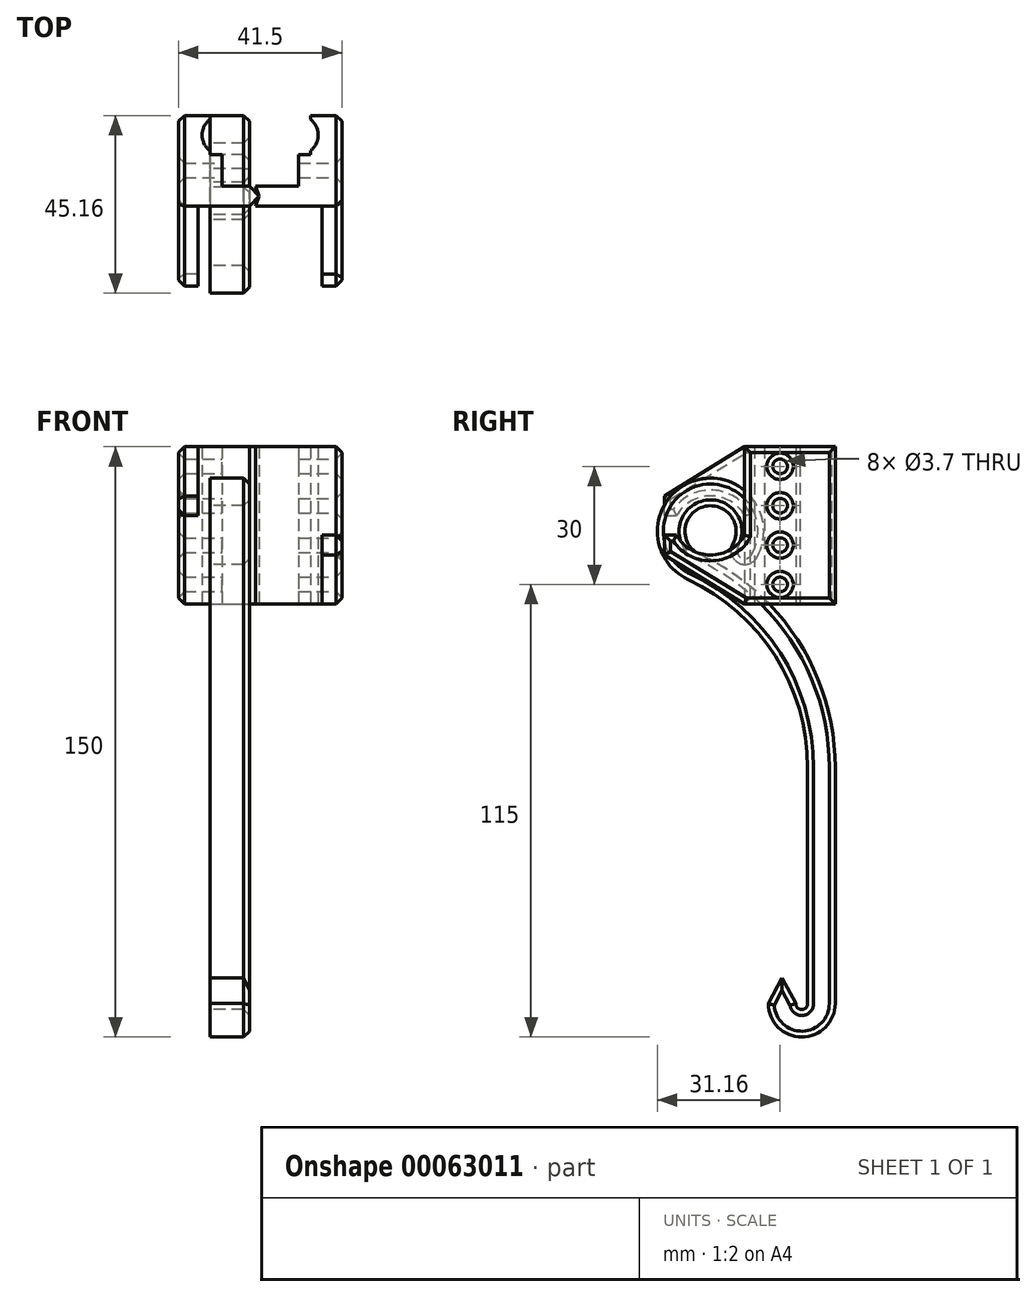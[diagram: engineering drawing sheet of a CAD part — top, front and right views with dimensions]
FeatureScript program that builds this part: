
annotation { "Feature Type Name" : "Feature", "Feature Type Description" : "" }
export const myFeature = defineFeature(function(context is Context, id is Id, definition is map)
    precondition{}
    {
        {
            var Q0;
            Q0=qCreatedBy(makeId("Top.planeOp"),FACE);
            var sketch = newSketch(context, id + "F0", { "sketchPlane" : qUnion([Q0])});
            skLineSegment(sketch, "E0", {"start": v(0, 0) * mm, "end": v(-50, 0) * mm, "construction": true});
            skLineSegment(sketch, "E1", {"start": v(-50, 0) * mm, "end": v(-50, 20) * mm, "construction": true});
            skLineSegment(sketch, "E2", {"start": v(-50, 20) * mm, "end": v(25.5, 20) * mm, "construction": true});
            skLineSegment(sketch, "E3", {"start": v(25.5, 20) * mm, "end": v(25.5, -10) * mm, "construction": true});
            skLineSegment(sketch, "E4", {"start": v(25.5, -10) * mm, "end": v(0, -10) * mm, "construction": true});
            skLineSegment(sketch, "E5", {"start": v(0, -10) * mm, "end": v(0, 0) * mm, "construction": true});
            skLineSegment(sketch, "E6", {"start": v(0, 0) * mm, "end": v(-8, 0) * mm});
            skLineSegment(sketch, "E7", {"start": v(-8, 0) * mm, "end": v(-8, -23) * mm});
            skLineSegment(sketch, "E8", {"start": v(-8, -23) * mm, "end": v(10, -23) * mm});
            skLineSegment(sketch, "E9", {"start": v(10, -23) * mm, "end": v(12.5, -20.5) * mm});
            skLineSegment(sketch, "E10", {"start": v(12.5, -20.5) * mm, "end": v(10, -18) * mm});
            skLineSegment(sketch, "E11", {"start": v(0, -10) * mm, "end": v(3, -10) * mm});
            skLineSegment(sketch, "E12", {"start": v(3, -10) * mm, "end": v(3, -18) * mm});
            skLineSegment(sketch, "E13", {"start": v(3, -18) * mm, "end": v(10, -18) * mm});
            skLineSegment(sketch, "E14", {"start": v(12.5, -20.5) * mm, "end": v(11.6, -18) * mm});
            skLineSegment(sketch, "E15", {"start": v(11.6, -18) * mm, "end": v(22.5, -18) * mm});
            skLineSegment(sketch, "E16", {"start": v(22.5, -18) * mm, "end": v(22.5, -10) * mm});
            skLineSegment(sketch, "E17", {"start": v(22.5, -10) * mm, "end": v(25.5, -10) * mm});
            skLineSegment(sketch, "E18", {"start": v(25.5, 0) * mm, "end": v(33.5, 0) * mm});
            skLineSegment(sketch, "E19", {"start": v(33.5, 0) * mm, "end": v(33.5, -23) * mm});
            skLineSegment(sketch, "E20", {"start": v(33.5, -23) * mm, "end": v(11.6, -23) * mm});
            skLineSegment(sketch, "E21", {"start": v(11.6, -23) * mm, "end": v(12.5, -20.5) * mm});
            skLineSegment(sketch, "E22", {"start": v(25.5, 0) * mm, "end": v(25.5, -1) * mm});
            skLineSegment(sketch, "E23", {"start": v(0, 0) * mm, "end": v(0, -1) * mm});
            skCircle(sketch, "E24", {"center": v(3, -5) * mm, "radius": 5 * mm, "construction": true});
            skCircle(sketch, "E25", {"center": v(22.5, -5) * mm, "radius": 5 * mm, "construction": true});
            skArc(sketch, "E26", {"start": v(0, -1) * mm, "mid": v(-2, -5) * mm, "end": v(0, -9) * mm});
            skArc(sketch, "E27", {"start": v(25.5, -9) * mm, "mid": v(27.5, -5) * mm, "end": v(25.5, -1) * mm});
            skLineSegment(sketch, "E28.trimOffspring", {"start": v(0, -9) * mm, "end": v(0, -10) * mm});
            skLineSegment(sketch, "E29.trimOffspring", {"start": v(25.5, -9) * mm, "end": v(25.5, -10) * mm});
            skSolve(sketch);
        }
        {
            var Q0;
            Q0 = qSketchRegion(id + "F0", true);
            extrude(context, id + "F1", {"entities" : qUnion([Q0]), "depth" : 40 * mm});
        }
        {
            var Q0;
            Q0=makeQuery(id+"F1.opExtrude","SWEPT_FACE",FACE,{"disambiguationData":[OSD([sQuery(id+"F0.wireOp",EDGE,"E19")])]});
            var sketch = newSketch(context, id + "F2", { "sketchPlane" : qUnion([Q0])});
            skArc(sketch, "E30", {"start": v(-40.32, 17.5) * mm, "mid": v(-31.66, 12.5) * mm, "end": v(-23, 17.5) * mm});
            skArc(sketch, "E31", {"start": v(-23, 22.5) * mm, "mid": v(-31.66, 27.5) * mm, "end": v(-40.32, 22.5) * mm});
            skLineSegment(sketch, "E32", {"start": v(-40.32, 17.5) * mm, "end": v(-31.66, 22.5) * mm, "construction": true});
            skLineSegment(sketch, "E33", {"start": v(-23, 17.5) * mm, "end": v(-31.66, 22.5) * mm, "construction": true});
            skLineSegment(sketch, "E34", {"start": v(-40.32, 17.5) * mm, "end": v(-43.32, 17.5) * mm});
            skLineSegment(sketch, "E35", {"start": v(-43.32, 17.5) * mm, "end": v(-43.32, 12.5) * mm});
            skLineSegment(sketch, "E36", {"start": v(-43.32, 12.5) * mm, "end": v(-23, 0) * mm});
            skLineSegment(sketch, "E37", {"start": v(-23, 0) * mm, "end": v(-23, 17.5) * mm});
            skLineSegment(sketch, "E38", {"start": v(-40.32, 22.5) * mm, "end": v(-43.32, 22.5) * mm});
            skLineSegment(sketch, "E39", {"start": v(-43.32, 22.5) * mm, "end": v(-43.32, 27.5) * mm});
            skLineSegment(sketch, "E40", {"start": v(-43.32, 27.5) * mm, "end": v(-23, 40) * mm});
            skPoint(sketch, "E41", {"position": v(-31.66, 27.5) * mm});
            skPoint(sketch, "E42", {"position": v(-31.66, 12.5) * mm});
            skLineSegment(sketch, "E43", {"start": v(-23, 22.5) * mm, "end": v(-23, 40) * mm});
            skSolve(sketch);
        }
        {
            var Q0;
            Q0=makeQuery(id+"F1.opExtrude","SWEPT_FACE",FACE,{"disambiguationData":[OSD([sQuery(id+"F0.wireOp",EDGE,"E7")])]});
            var sketch = newSketch(context, id + "F3", { "sketchPlane" : qUnion([Q0])});
            skLineSegment(sketch, "E44.0", {"start": v(23, 22.5) * mm, "end": v(23, 40) * mm});
            skLineSegment(sketch, "E44.1", {"start": v(43.32, 27.5) * mm, "end": v(23, 40) * mm});
            skArc(sketch, "E44.2", {"start": v(23, 22.5) * mm, "mid": v(31.66, 27.5) * mm, "end": v(40.32, 22.5) * mm});
            skLineSegment(sketch, "E44.3", {"start": v(40.32, 22.5) * mm, "end": v(43.32, 22.5) * mm});
            skLineSegment(sketch, "E44.4", {"start": v(43.32, 22.5) * mm, "end": v(43.32, 27.5) * mm});
            skSolve(sketch);
        }
        {
            var Q0;
            Q0 = qSketchRegion(id + "F3", true);
            extrude(context, id + "F4", {"entities" : qUnion([Q0]), "operationType" : NewBodyOperationType.ADD, "oppositeDirection" : true, "depth" : 5 * mm});
        }
        {
            var Q0;
            Q0=makeQuery(id+"F2.imprint","IMPRINT",FACE,{"disambiguationData":[TD([[makeQuery(id+"F2.imprint","IMPRINT",EDGE,{"derivedFrom":sQuery(id+"F2.wireOp",EDGE,"E30")}),-1.0]])]});
            var Q1;
            Q1=sQuery(id+"F2.wireOp",EDGE,"E30");
            var Q2;
            Q2=sQuery(id+"F2.wireOp",EDGE,"E34");
            var Q3;
            Q3=sQuery(id+"F2.wireOp",EDGE,"E35");
            var Q4;
            Q4=sQuery(id+"F2.wireOp",EDGE,"E36");
            var Q5;
            Q5=sQuery(id+"F2.wireOp",EDGE,"E37");
            extrude(context, id + "F5", {"entities" : qUnion([Q0]), "operationType" : NewBodyOperationType.ADD, "surfaceEntities" : qUnion([Q1, Q2, Q3, Q4, Q5]), "oppositeDirection" : true, "depth" : 5 * mm});
        }
        {
            var Q0;
            Q0=makeQuery(id+"F1.opExtrude","SWEPT_FACE",FACE,{"disambiguationData":[OSD([sQuery(id+"F0.wireOp",EDGE,"E12")])]});
            var sketch = newSketch(context, id + "F6", { "sketchPlane" : qUnion([Q0])});
            skCircle(sketch, "E45", {"center": v(-14, 35) * mm, "radius": 1.85 * mm});
            skCircle(sketch, "E46", {"center": v(-14, 25) * mm, "radius": 1.85 * mm});
            skCircle(sketch, "E47", {"center": v(-14, 15) * mm, "radius": 1.85 * mm});
            skCircle(sketch, "E48", {"center": v(-14, 5) * mm, "radius": 1.85 * mm});
            skLineSegment(sketch, "E49", {"start": v(-14, 0) * mm, "end": v(-14, 5) * mm, "construction": true});
            skLineSegment(sketch, "E50", {"start": v(-14, 15) * mm, "end": v(-14, 5) * mm, "construction": true});
            skLineSegment(sketch, "E51", {"start": v(-14, 15) * mm, "end": v(-14, 25) * mm, "construction": true});
            skLineSegment(sketch, "E52", {"start": v(-14, 35) * mm, "end": v(-14, 25) * mm, "construction": true});
            skLineSegment(sketch, "E53", {"start": v(-14, 35) * mm, "end": v(-14, 40) * mm, "construction": true});
            skSolve(sketch);
        }
        {
            var Q0;
            Q0 = qSketchRegion(id + "F6", true);
            extrude(context, id + "F7", {"entities" : qUnion([Q0]), "operationType" : NewBodyOperationType.REMOVE, "endBound" : BoundingType.THROUGH_ALL, "oppositeDirection" : true, "depth" : 25 * mm, "hasSecondDirection" : true, "secondDirectionBound" : SecondDirectionBoundingType.THROUGH_ALL, "secondDirectionOppositeDirection" : false, "secondDirectionDepth" : 25 * mm});
        }
        {
            var Q0;
            Q0=makeQuery(id+"F5.boolean.opBoolean","MERGE",FACE,{"derivedFrom":[makeQuery(id+"F1.opExtrude","SWEPT_FACE",FACE,{"disambiguationData":[OSD([sQuery(id+"F0.wireOp",EDGE,"E19")])]}),makeQuery(id+"F5.opExtrude","CAP_FACE",FACE,{"disambiguationData":[OSD([sQuery(id+"F2.wireOp",EDGE,"E30"),sQuery(id+"F2.wireOp",EDGE,"E34"),sQuery(id+"F2.wireOp",EDGE,"E35"),sQuery(id+"F2.wireOp",EDGE,"E36"),sQuery(id+"F2.wireOp",EDGE,"E37")])],"isStart":true})]});
            var Q1;
            Q1=makeQuery(id+"F4.boolean.opBoolean","MERGE",FACE,{"derivedFrom":[makeQuery(id+"F1.opExtrude","SWEPT_FACE",FACE,{"disambiguationData":[OSD([sQuery(id+"F0.wireOp",EDGE,"E7")])]}),makeQuery(id+"F4.opExtrude","CAP_FACE",FACE,{"disambiguationData":[OSD([sQuery(id+"F3.wireOp",EDGE,"E44.0"),sQuery(id+"F3.wireOp",EDGE,"E44.1"),sQuery(id+"F3.wireOp",EDGE,"E44.2"),sQuery(id+"F3.wireOp",EDGE,"E44.3"),sQuery(id+"F3.wireOp",EDGE,"E44.4")])],"isStart":true})]});
            chamfer(context, id + "F8", {"entities" : qUnion([Q0, Q1]), "width" : 1.5 * mm, "tangentPropagation" : true});
        }
        {
            var Q0;
            Q0=qCreatedBy(makeId("Right.planeOp"),FACE);
            var sketch = newSketch(context, id + "F9", { "sketchPlane" : qUnion([Q0])});
            skCircle(sketch, "E54", {"center": v(-31.66, 18.5) * mm, "radius": 6 * mm});
            skPoint(sketch, "E55", {"position": v(-31.66, 12.5) * mm});
            skLineSegment(sketch, "E56", {"start": v(-40.32, 17.5) * mm, "end": v(-23, 17.5) * mm, "construction": true});
            skPoint(sketch, "E57", {"position": v(-31.66, 17.5) * mm});
            skArc(sketch, "E58", {"start": v(-19.91, 11.85) * mm, "mid": v(-35.76, 31.36) * mm, "end": v(-37.38, 6.27) * mm});
            skArc(sketch, "E59", {"start": v(-26, 15.3) * mm, "mid": v(-33.64, 24.7) * mm, "end": v(-34.42, 12.61) * mm});
            skArc(sketch, "E60", {"start": v(-37.38, 6.27) * mm, "mid": v(-15.24, -13.2) * mm, "end": v(-7, -41.5) * mm});
            skArc(sketch, "E61", {"start": v(-34.42, 12.61) * mm, "mid": v(-9.33, -9.43) * mm, "end": v(0, -41.5) * mm});
            skArc(sketch, "E62", {"start": v(-19.91, 11.85) * mm, "mid": v(-24.68, 10.53) * mm, "end": v(-26, 15.3) * mm});
            skLineSegment(sketch, "E63", {"start": v(0, -41.5) * mm, "end": v(0, -101.5) * mm});
            skLineSegment(sketch, "E64", {"start": v(-7, -41.5) * mm, "end": v(-7, -101.5) * mm});
            skArc(sketch, "E65", {"start": v(-10, -101.5) * mm, "mid": v(-8.5, -103) * mm, "end": v(-7, -101.5) * mm});
            skArc(sketch, "E66", {"start": v(-17, -101.5) * mm, "mid": v(-8.5, -110) * mm, "end": v(0, -101.5) * mm});
            skPoint(sketch, "E67", {"position": v(-8.5, -110) * mm});
            skPoint(sketch, "E68", {"position": v(-24.68, 10.53) * mm});
            skLineSegment(sketch, "E69", {"start": v(-22.96, 13.57) * mm, "end": v(-24.68, 10.53) * mm, "construction": true});
            skLineSegment(sketch, "E70", {"start": v(-24.68, 10.53) * mm, "end": v(-26.16, 7.92) * mm, "construction": true});
            skPoint(sketch, "E71", {"position": v(-31.66, 32) * mm});
            skLineSegment(sketch, "E72", {"start": v(-17, -101.5) * mm, "end": v(-13.5, -95) * mm});
            skLineSegment(sketch, "E73", {"start": v(-13.5, -95) * mm, "end": v(-10, -101.5) * mm});
            skSolve(sketch);
        }
        {
            var Q0;
            Q0=makeQuery(id+"F9.imprint","IMPRINT",FACE,{"disambiguationData":[TD([[makeQuery(id+"F9.imprint","IMPRINT",EDGE,{"derivedFrom":sQuery(id+"F9.wireOp",EDGE,"E58")}),1.0]])]});
            extrude(context, id + "F10", {"entities" : qUnion([Q0]), "depth" : 10 * mm});
        }
        {
            var Q0;
            Q0=makeQuery(id+"F10.opExtrude","CAP_FACE",FACE,{"disambiguationData":[OSD([sQuery(id+"F9.wireOp",EDGE,"E58"),sQuery(id+"F9.wireOp",EDGE,"E59"),sQuery(id+"F9.wireOp",EDGE,"E60"),sQuery(id+"F9.wireOp",EDGE,"E61"),sQuery(id+"F9.wireOp",EDGE,"E62"),sQuery(id+"F9.wireOp",EDGE,"E63"),sQuery(id+"F9.wireOp",EDGE,"E64"),sQuery(id+"F9.wireOp",EDGE,"E65"),sQuery(id+"F9.wireOp",EDGE,"E66"),sQuery(id+"F9.wireOp",EDGE,"E72"),sQuery(id+"F9.wireOp",EDGE,"E73")])],"isStart":false});
            chamfer(context, id + "F11", {"entities" : qUnion([Q0]), "width" : 1.5 * mm, "tangentPropagation" : true});
        }
    });
